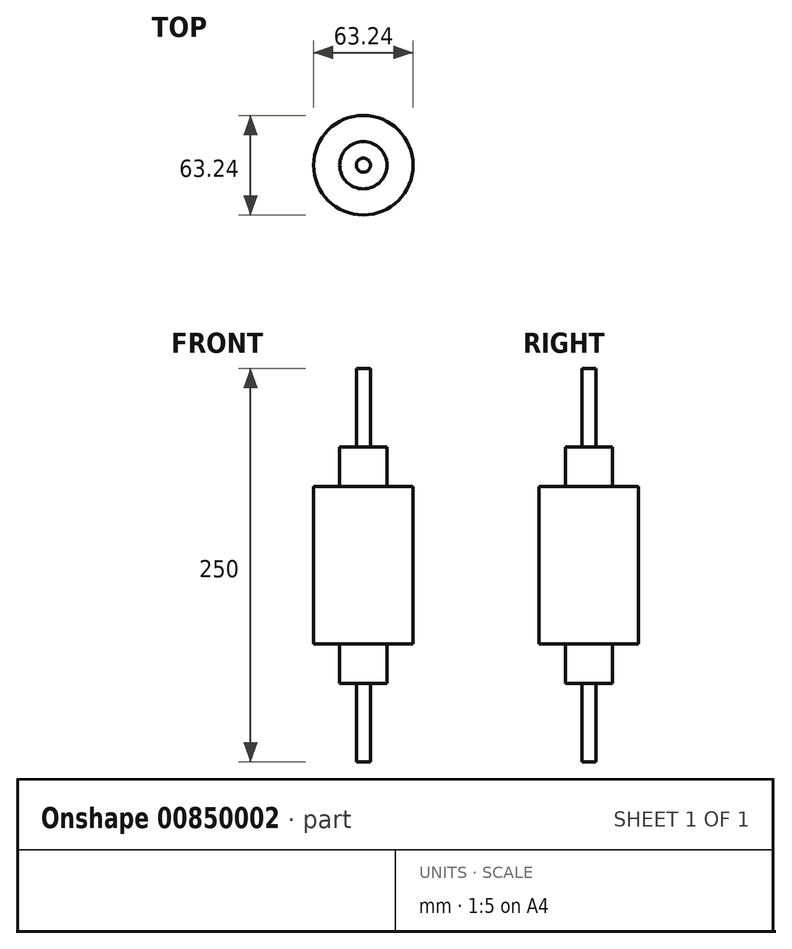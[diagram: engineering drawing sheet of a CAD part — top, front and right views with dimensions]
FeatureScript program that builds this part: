
annotation { "Feature Type Name" : "Feature", "Feature Type Description" : "" }
export const myFeature = defineFeature(function(context is Context, id is Id, definition is map)
    precondition{}
    {
        {
            var Q0;
            Q0=qCreatedBy(makeId("Top.planeOp"),FACE);
            var sketch = newSketch(context, id + "F0", { "sketchPlane" : qUnion([Q0])});
            skCircle(sketch, "E0", {"center": v(0, 0) * mm, "radius": 31.62 * mm});
            skSolve(sketch);
        }
        {
            var Q0;
            Q0=makeQuery(id+"F0.imprint","IMPRINT",FACE,{"disambiguationData":[TD([[makeQuery(id+"F0.imprint","IMPRINT",EDGE,{"derivedFrom":sQuery(id+"F0.wireOp",EDGE,"E0")}),1.0]])]});
            extrude(context, id + "F1", {"entities" : qUnion([Q0]), "depth" : 100 * mm, "offsetDistance" : 25 * mm});
        }
        {
            var Q0;
            Q0=makeQuery(id+"F1.opExtrude","CAP_FACE",FACE,{"disambiguationData":[OSD([sQuery(id+"F0.wireOp",EDGE,"E0")])],"isStart":false});
            var sketch = newSketch(context, id + "F2", { "sketchPlane" : qUnion([Q0])});
            skCircle(sketch, "E1", {"center": v(0, 0) * mm, "radius": 15 * mm});
            skSolve(sketch);
        }
        {
            var Q0;
            Q0=makeQuery(id+"F2.imprint","IMPRINT",FACE,{"disambiguationData":[TD([[makeQuery(id+"F2.imprint","IMPRINT",EDGE,{"derivedFrom":sQuery(id+"F2.wireOp",EDGE,"E1")}),1.0]])]});
            extrude(context, id + "F3", {"entities" : qUnion([Q0]), "operationType" : NewBodyOperationType.ADD, "depth" : 25 * mm, "offsetDistance" : 25 * mm});
        }
        {
            var Q0;
            Q0=makeQuery(id+"F3.opExtrude","CAP_FACE",FACE,{"disambiguationData":[OSD([sQuery(id+"F2.wireOp",EDGE,"E1")])],"isStart":false});
            var sketch = newSketch(context, id + "F4", { "sketchPlane" : qUnion([Q0])});
            skCircle(sketch, "E2", {"center": v(0, 0) * mm, "radius": 4.5 * mm});
            skSolve(sketch);
        }
        {
            var Q0;
            Q0=makeQuery(id+"F4.imprint","IMPRINT",FACE,{"disambiguationData":[TD([[makeQuery(id+"F4.imprint","IMPRINT",EDGE,{"derivedFrom":sQuery(id+"F4.wireOp",EDGE,"E2")}),1.0]])]});
            extrude(context, id + "F5", {"entities" : qUnion([Q0]), "operationType" : NewBodyOperationType.ADD, "depth" : 50 * mm, "offsetDistance" : 25 * mm});
        }
        {
            var Q0;
            Q0=makeQuery(id+"F1.opExtrude","CAP_FACE",FACE,{"disambiguationData":[OSD([sQuery(id+"F0.wireOp",EDGE,"E0")])],"isStart":true});
            var sketch = newSketch(context, id + "F6", { "sketchPlane" : qUnion([Q0])});
            skCircle(sketch, "E3", {"center": v(0, 0) * mm, "radius": 15 * mm});
            skSolve(sketch);
        }
        {
            var Q0;
            Q0=makeQuery(id+"F6.imprint","IMPRINT",FACE,{"disambiguationData":[TD([[makeQuery(id+"F6.imprint","IMPRINT",EDGE,{"derivedFrom":sQuery(id+"F6.wireOp",EDGE,"E3")}),1.0]])]});
            extrude(context, id + "F7", {"entities" : qUnion([Q0]), "operationType" : NewBodyOperationType.ADD, "depth" : 25 * mm, "offsetDistance" : 25 * mm});
        }
        {
            var Q0;
            Q0=makeQuery(id+"F7.opExtrude","CAP_FACE",FACE,{"disambiguationData":[OSD([sQuery(id+"F6.wireOp",EDGE,"E3")])],"isStart":false});
            var sketch = newSketch(context, id + "F8", { "sketchPlane" : qUnion([Q0])});
            skCircle(sketch, "E4", {"center": v(0, 0) * mm, "radius": 4.5 * mm});
            skSolve(sketch);
        }
        {
            var Q0;
            Q0=makeQuery(id+"F8.imprint","IMPRINT",FACE,{"disambiguationData":[TD([[makeQuery(id+"F8.imprint","IMPRINT",EDGE,{"derivedFrom":sQuery(id+"F8.wireOp",EDGE,"E4")}),1.0]])]});
            extrude(context, id + "F9", {"entities" : qUnion([Q0]), "operationType" : NewBodyOperationType.ADD, "depth" : 50 * mm, "offsetDistance" : 25 * mm});
        }
    });
